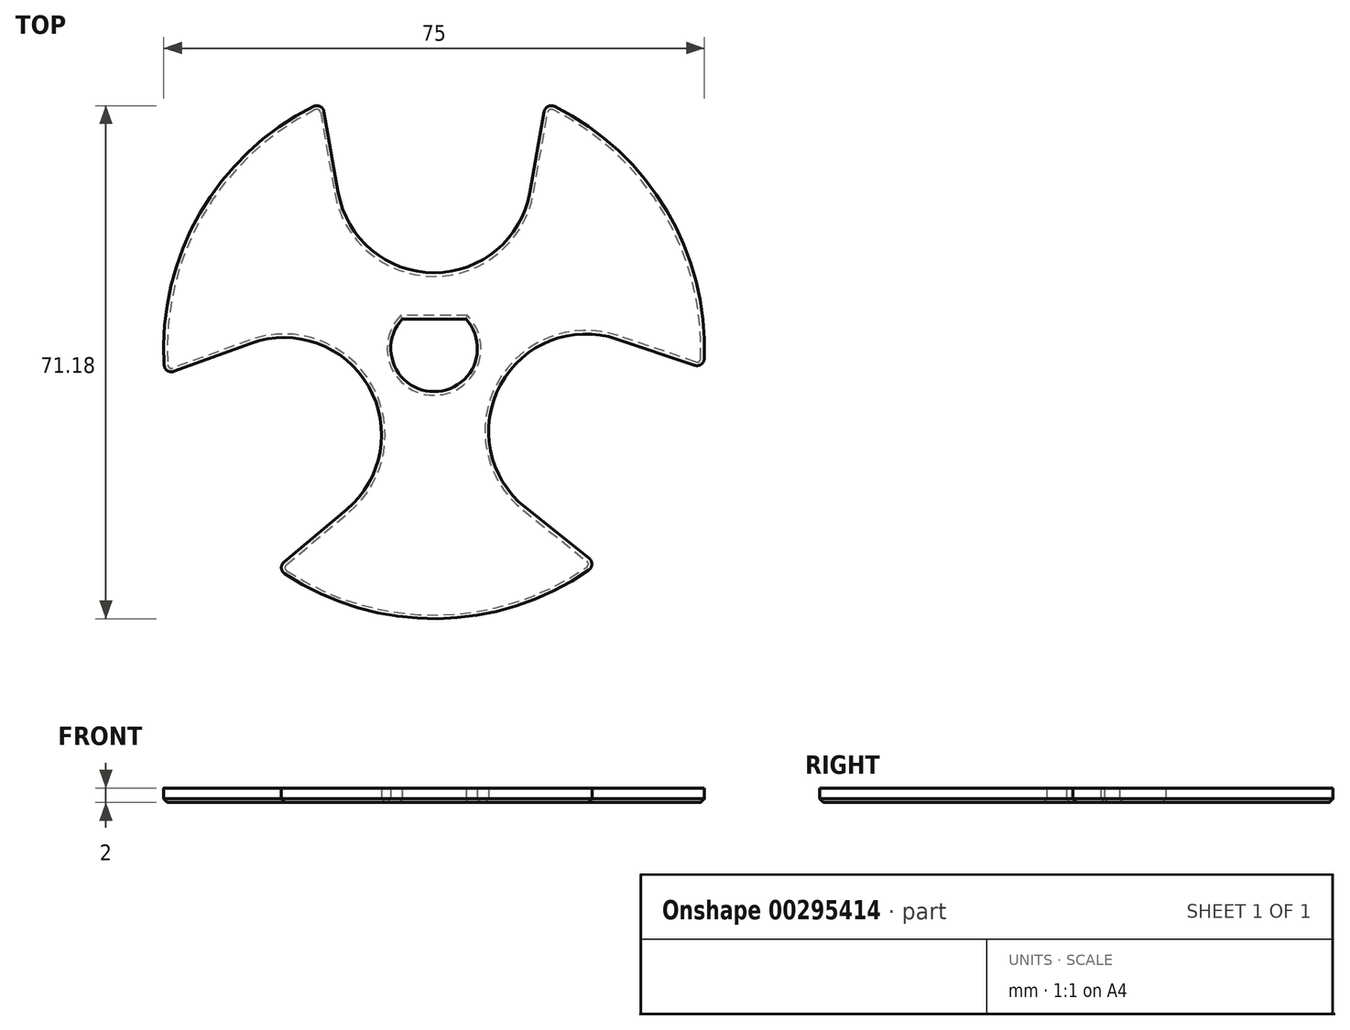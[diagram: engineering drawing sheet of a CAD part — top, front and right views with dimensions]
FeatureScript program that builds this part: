
annotation { "Feature Type Name" : "Feature", "Feature Type Description" : "" }
export const myFeature = defineFeature(function(context is Context, id is Id, definition is map)
    precondition{}
    {
        {
            var Q0;
            Q0=qCreatedBy(makeId("Top.planeOp"),FACE);
            var sketch = newSketch(context, id + "F0", { "sketchPlane" : qUnion([Q0])});
            skArc(sketch, "E0", {"start": v(-15.5, 34.15) * mm, "mid": v(-32.48, 18.75) * mm, "end": v(-37.32, -3.65) * mm});
            skLineSegment(sketch, "E1", {"start": v(0, 0) * mm, "end": v(32.25, 19.13) * mm, "construction": true});
            skLineSegment(sketch, "E2", {"start": v(0, 0) * mm, "end": v(-32.48, 18.75) * mm, "construction": true});
            skLineSegment(sketch, "E3", {"start": v(0, 0) * mm, "end": v(0, -37.5) * mm, "construction": true});
            skLineSegment(sketch, "E4", {"start": v(0, 0) * mm, "end": v(0, 37.5) * mm, "construction": true});
            skArc(sketch, "E5", {"start": v(-13.3, 21.66) * mm, "mid": v(0, 10.5) * mm, "end": v(13.3, 21.66) * mm});
            skLineSegment(sketch, "E6", {"start": v(0, 24) * mm, "end": v(13.3, 21.66) * mm, "construction": true});
            skLineSegment(sketch, "E7", {"start": v(13.3, 21.66) * mm, "end": v(15.5, 34.15) * mm});
            skLineSegment(sketch, "E8.MirrorCS", {"start": v(-13.3, 21.66) * mm, "end": v(-15.5, 34.15) * mm});
            skLineSegment(sketch, "E9.MirrorCS", {"start": v(25.38, 1.29) * mm, "end": v(37.4, -2.76) * mm});
            skArc(sketch, "E10.MirrorCS", {"start": v(12.63, -22.05) * mm, "mid": v(9.22, -5.03) * mm, "end": v(25.38, 1.29) * mm});
            skLineSegment(sketch, "E11.MirrorCS", {"start": v(12.63, -22.05) * mm, "end": v(22.54, -29.97) * mm});
            skArc(sketch, "E12.MirrorCS", {"start": v(-25.4, 0.69) * mm, "mid": v(-9.1, -5.25) * mm, "end": v(-12.1, -22.34) * mm});
            skLineSegment(sketch, "E13.MirrorCS", {"start": v(-25.4, 0.69) * mm, "end": v(-37.32, -3.65) * mm});
            skLineSegment(sketch, "E14.MirrorCS", {"start": v(-12.1, -22.34) * mm, "end": v(-21.82, -30.5) * mm});
            skArc(sketch, "E15.trimOffspring", {"start": v(37.4, -2.76) * mm, "mid": v(32.25, 19.13) * mm, "end": v(15.5, 34.15) * mm});
            skArc(sketch, "E16.trimOffspring", {"start": v(-21.82, -30.5) * mm, "mid": v(0.45, -37.5) * mm, "end": v(22.54, -29.97) * mm});
            skArc(sketch, "E17", {"start": v(-4.36, 3.9) * mm, "mid": v(0, -5.85) * mm, "end": v(4.36, 3.9) * mm, "construction": true});
            skLineSegment(sketch, "E18", {"start": v(-4.36, 3.9) * mm, "end": v(4.36, 3.9) * mm, "construction": true});
            skLineSegment(sketch, "E19.0", {"start": v(-4.43, 4.05) * mm, "end": v(4.43, 4.05) * mm});
            skArc(sketch, "E20.0", {"start": v(-4.43, 4.05) * mm, "mid": v(0, -6) * mm, "end": v(4.43, 4.05) * mm});
            skSolve(sketch);
        }
        {
            var Q0;
            Q0 = qSketchRegion(id + "F0", true);
            extrude(context, id + "F1", {"entities" : qUnion([Q0]), "depth" : 2 * mm});
        }
        {
            var Q0;
            Q0=makeQuery(id+"F1.opExtrude","SWEPT_EDGE",EDGE,{"disambiguationData":[OSD([sQuery(id+"F0.wireOp",EDGE,"E11.MirrorCS"),sQuery(id+"F0.wireOp",EDGE,"E16.trimOffspring")])]});
            var Q1;
            Q1=makeQuery(id+"F1.opExtrude","SWEPT_EDGE",EDGE,{"disambiguationData":[OSD([sQuery(id+"F0.wireOp",EDGE,"E9.MirrorCS"),sQuery(id+"F0.wireOp",EDGE,"E15.trimOffspring")])]});
            var Q2;
            Q2=makeQuery(id+"F1.opExtrude","SWEPT_EDGE",EDGE,{"disambiguationData":[OSD([sQuery(id+"F0.wireOp",EDGE,"E14.MirrorCS"),sQuery(id+"F0.wireOp",EDGE,"E16.trimOffspring")])]});
            var Q3;
            Q3=makeQuery(id+"F1.opExtrude","SWEPT_EDGE",EDGE,{"disambiguationData":[OSD([sQuery(id+"F0.wireOp",EDGE,"E0"),sQuery(id+"F0.wireOp",EDGE,"E13.MirrorCS")])]});
            var Q4;
            Q4=makeQuery(id+"F1.opExtrude","SWEPT_EDGE",EDGE,{"disambiguationData":[OSD([sQuery(id+"F0.wireOp",EDGE,"E0"),sQuery(id+"F0.wireOp",EDGE,"E8.MirrorCS")])]});
            var Q5;
            Q5=makeQuery(id+"F1.opExtrude","SWEPT_EDGE",EDGE,{"disambiguationData":[OSD([sQuery(id+"F0.wireOp",EDGE,"E7"),sQuery(id+"F0.wireOp",EDGE,"E15.trimOffspring")])]});
            fillet(context, id + "F2", {"entities" : qUnion([Q0, Q1, Q2, Q3, Q4, Q5]), "radius" : 1 * mm, "tangentPropagation" : true, "allowEdgeOverflow" : false});
        }
        {
            var Q0;
            Q0=makeQuery(id+"F1.opExtrude","CAP_FACE",FACE,{"disambiguationData":[OSD([sQuery(id+"F0.wireOp",EDGE,"E0"),sQuery(id+"F0.wireOp",EDGE,"E5"),sQuery(id+"F0.wireOp",EDGE,"E7"),sQuery(id+"F0.wireOp",EDGE,"E8.MirrorCS"),sQuery(id+"F0.wireOp",EDGE,"E9.MirrorCS"),sQuery(id+"F0.wireOp",EDGE,"E10.MirrorCS"),sQuery(id+"F0.wireOp",EDGE,"E11.MirrorCS"),sQuery(id+"F0.wireOp",EDGE,"E12.MirrorCS"),sQuery(id+"F0.wireOp",EDGE,"E13.MirrorCS"),sQuery(id+"F0.wireOp",EDGE,"E14.MirrorCS"),sQuery(id+"F0.wireOp",EDGE,"E15.trimOffspring"),sQuery(id+"F0.wireOp",EDGE,"E16.trimOffspring"),sQuery(id+"F0.wireOp",EDGE,"E19.0"),sQuery(id+"F0.wireOp",EDGE,"E20.0")])],"isStart":true});
            chamfer(context, id + "F3", {"entities" : qUnion([Q0]), "width" : 0.5 * mm, "tangentPropagation" : true});
        }
    });
